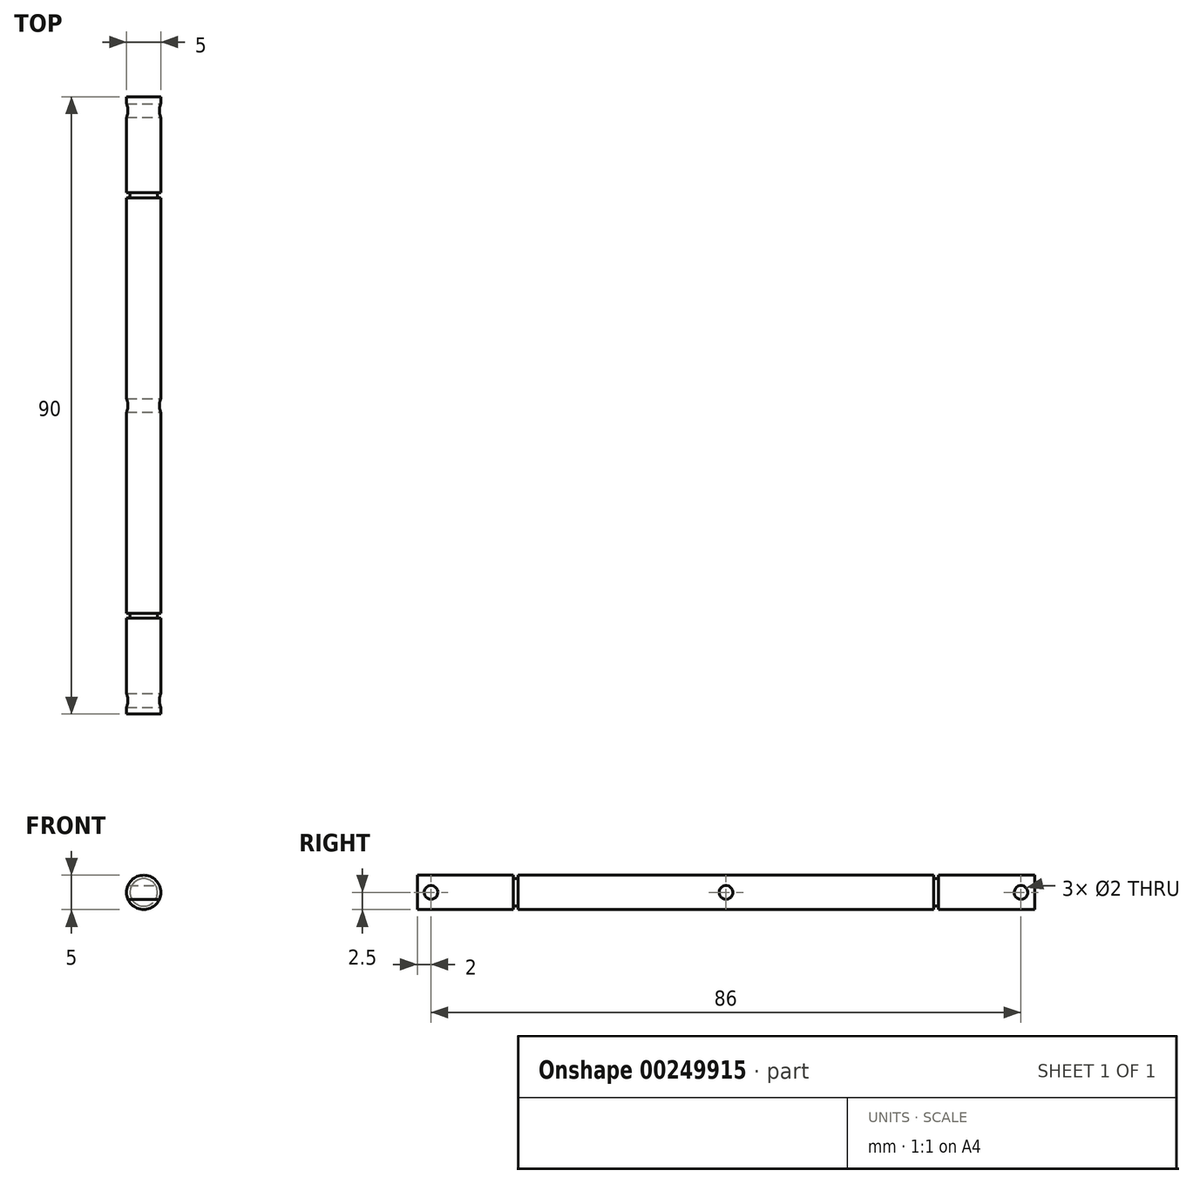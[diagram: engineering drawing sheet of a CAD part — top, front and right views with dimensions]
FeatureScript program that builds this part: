
annotation { "Feature Type Name" : "Feature", "Feature Type Description" : "" }
export const myFeature = defineFeature(function(context is Context, id is Id, definition is map)
    precondition{}
    {
        {
            var Q0;
            Q0=qCreatedBy(makeId("Front.planeOp"),FACE);
            var sketch = newSketch(context, id + "F0", { "sketchPlane" : qUnion([Q0])});
            skCircle(sketch, "E0", {"center": v(0, 0) * mm, "radius": 2.5 * mm});
            skSolve(sketch);
        }
        {
            var Q0;
            Q0=makeQuery(id+"F0.imprint","IMPRINT",FACE,{"disambiguationData":[TD([[makeQuery(id+"F0.imprint","IMPRINT",EDGE,{"derivedFrom":sQuery(id+"F0.wireOp",EDGE,"E0")}),1.0]])]});
            extrude(context, id + "F1", {"entities" : qUnion([Q0]), "endBound" : BoundingType.SYMMETRIC, "depth" : 90 * mm});
        }
        {
            var Q0;
            Q0=qCreatedBy(makeId("Right.planeOp"),FACE);
            var sketch = newSketch(context, id + "F2", { "sketchPlane" : qUnion([Q0])});
            skLineSegment(sketch, "E1", {"start": v(-31, 2.5) * mm, "end": v(-30.3, 2.5) * mm});
            skLineSegment(sketch, "E2", {"start": v(31, 2.5) * mm, "end": v(31, 2) * mm});
            skLineSegment(sketch, "E3", {"start": v(31, 2) * mm, "end": v(30.3, 2) * mm});
            skLineSegment(sketch, "E4", {"start": v(30.3, 2) * mm, "end": v(30.3, 2.5) * mm});
            skLineSegment(sketch, "E5.MirrorCS", {"start": v(-31, 2) * mm, "end": v(-30.3, 2) * mm});
            skLineSegment(sketch, "E6.MirrorCS", {"start": v(-30.3, 2) * mm, "end": v(-30.3, 2.5) * mm});
            skLineSegment(sketch, "E7.MirrorCS", {"start": v(-31, 2.5) * mm, "end": v(-31, 2) * mm});
            skLineSegment(sketch, "E8.trimOffspring", {"start": v(30.3, 2.5) * mm, "end": v(31, 2.5) * mm});
            skSolve(sketch);
        }
        {
            var Q0;
            Q0=qCreatedBy(makeId("Right.planeOp"),FACE);
            var sketch = newSketch(context, id + "F3", { "sketchPlane" : qUnion([Q0])});
            skLineSegment(sketch, "E9", {"start": v(-55.83, 0) * mm, "end": v(49.23, 0) * mm, "construction": true});
            skSolve(sketch);
        }
        {
            var Q0;
            Q0 = qSketchRegion(id + "F2", true);
            var Q1;
            Q1=sQuery(id+"F3.wireOp",EDGE,"E9");
            revolve(context, id + "F4", {"operationType" : NewBodyOperationType.REMOVE, "entities" : qUnion([Q0]), "axis" : qUnion([Q1]), "revolveType" : RevolveType.FULL, "oppositeDirection" : true});
        }
        {
            var Q0;
            Q0=qCreatedBy(makeId("Right.planeOp"),FACE);
            var sketch = newSketch(context, id + "F5", { "sketchPlane" : qUnion([Q0])});
            skCircle(sketch, "E10", {"center": v(-43, 0) * mm, "radius": 1 * mm});
            skCircle(sketch, "E11", {"center": v(43, 0) * mm, "radius": 1 * mm});
            skCircle(sketch, "E12", {"center": v(0, 0) * mm, "radius": 1 * mm});
            skSolve(sketch);
        }
        {
            var Q0;
            Q0 = qSketchRegion(id + "F5", true);
            extrude(context, id + "F6", {"entities" : qUnion([Q0]), "operationType" : NewBodyOperationType.REMOVE, "endBound" : BoundingType.SYMMETRIC, "oppositeDirection" : true, "depth" : 25 * mm});
        }
        {
            var Q0;
            Q0=makeQuery(id+"F4.boolean.opBoolean","COPY",EDGE,{"derivedFrom":makeQuery(id+"F4.opRevolve","SWEPT_EDGE",EDGE,{"disambiguationData":[OSD([sQuery(id+"F2.wireOp",EDGE,"E5.MirrorCS"),sQuery(id+"F2.wireOp",EDGE,"E7.MirrorCS")])]})});
            var Q1;
            Q1=makeQuery(id+"F4.boolean.opBoolean","COPY",EDGE,{"derivedFrom":makeQuery(id+"F4.opRevolve","SWEPT_EDGE",EDGE,{"disambiguationData":[OSD([sQuery(id+"F2.wireOp",EDGE,"E5.MirrorCS"),sQuery(id+"F2.wireOp",EDGE,"E6.MirrorCS")])]})});
            var Q2;
            Q2=makeQuery(id+"F4.boolean.opBoolean","COPY",EDGE,{"derivedFrom":makeQuery(id+"F4.opRevolve","SWEPT_EDGE",EDGE,{"disambiguationData":[OSD([sQuery(id+"F2.wireOp",EDGE,"E3"),sQuery(id+"F2.wireOp",EDGE,"E4")])]})});
            var Q3;
            Q3=makeQuery(id+"F4.boolean.opBoolean","COPY",EDGE,{"derivedFrom":makeQuery(id+"F4.opRevolve","SWEPT_EDGE",EDGE,{"disambiguationData":[OSD([sQuery(id+"F2.wireOp",EDGE,"E2"),sQuery(id+"F2.wireOp",EDGE,"E3")])]})});
            fillet(context, id + "F7", {"entities" : qUnion([Q0, Q1, Q2, Q3]), "radius" : .25 * mm, "tangentPropagation" : true, "allowEdgeOverflow" : false});
        }
    });
